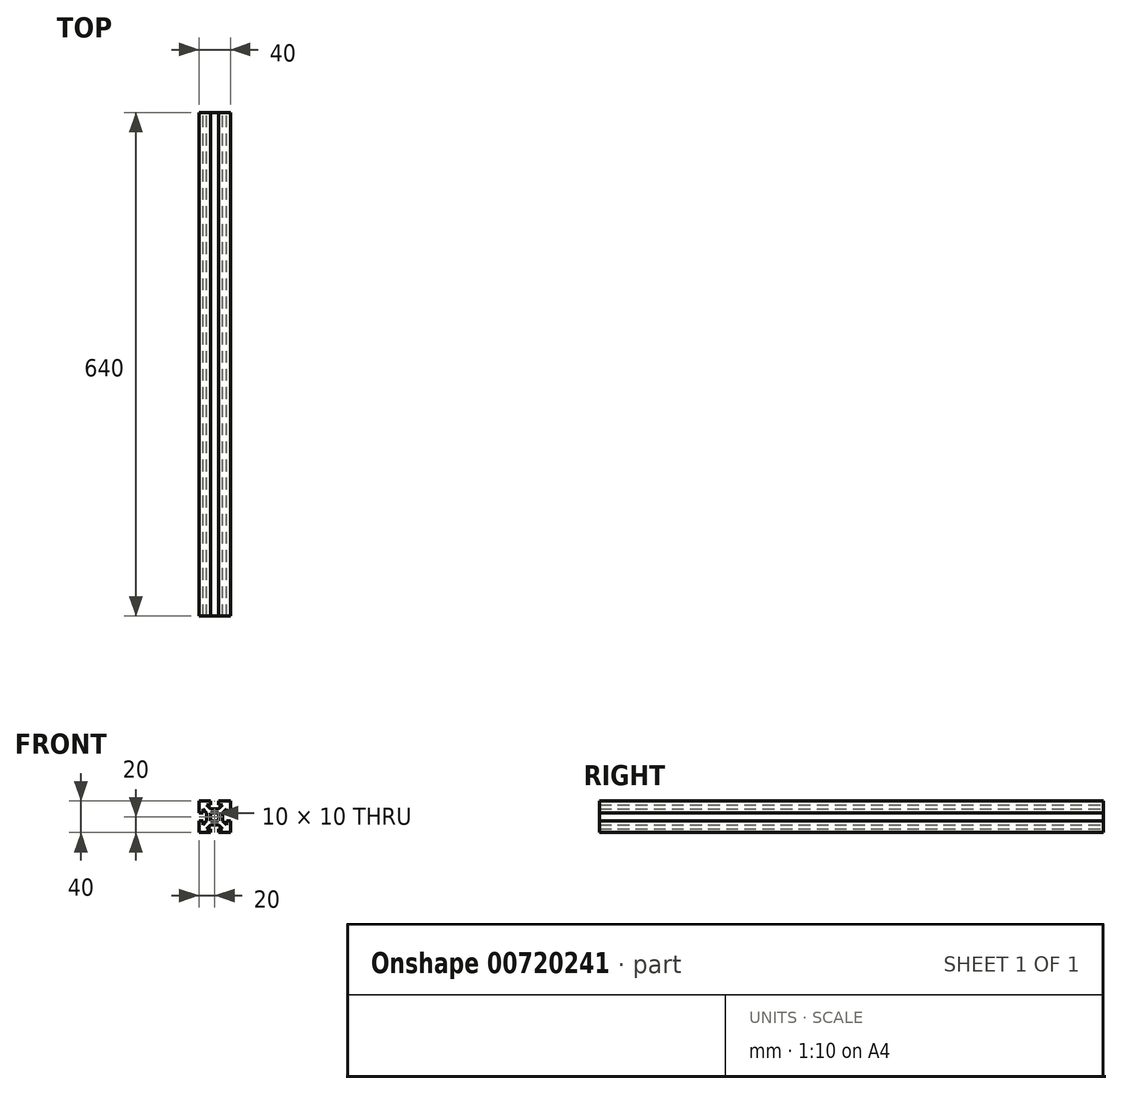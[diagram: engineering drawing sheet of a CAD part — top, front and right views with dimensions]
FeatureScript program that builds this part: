
annotation { "Feature Type Name" : "Feature", "Feature Type Description" : "" }
export const myFeature = defineFeature(function(context is Context, id is Id, definition is map)
    precondition{}
    {
        {
            var Q0;
            Q0=qCreatedBy(makeId("Front.planeOp"),FACE);
            var sketch = newSketch(context, id + "F0", { "sketchPlane" : qUnion([Q0])});
            skLineSegment(sketch, "E0.bottom", {"start": v(20, 20) * mm, "end": v(5, 20) * mm});
            skLineSegment(sketch, "E0.top", {"start": v(20, -20) * mm, "end": v(5, -20) * mm});
            skLineSegment(sketch, "E0.left", {"start": v(20, 20) * mm, "end": v(20, 5) * mm});
            skLineSegment(sketch, "E0.right", {"start": v(-20, 20) * mm, "end": v(-20, 5) * mm});
            skPoint(sketch, "E0.middle", {"position": v(0, 0) * mm});
            skLineSegment(sketch, "E1", {"start": v(0, 20) * mm, "end": v(0, -20) * mm, "construction": true});
            skLineSegment(sketch, "E2", {"start": v(-20, 0) * mm, "end": v(20, 0) * mm, "construction": true});
            skLineSegment(sketch, "E3", {"start": v(-20, 5) * mm, "end": v(-15, 5) * mm});
            skLineSegment(sketch, "E4", {"start": v(-20, -5) * mm, "end": v(-15, -5) * mm});
            skLineSegment(sketch, "E5", {"start": v(-5, 20) * mm, "end": v(-5, 15) * mm});
            skLineSegment(sketch, "E6", {"start": v(5, 20) * mm, "end": v(5, 15) * mm});
            skLineSegment(sketch, "E7", {"start": v(-10, 15) * mm, "end": v(-5, 15) * mm});
            skLineSegment(sketch, "E8", {"start": v(-10, -15) * mm, "end": v(-5, -15) * mm});
            skLineSegment(sketch, "E9", {"start": v(15, 10) * mm, "end": v(15, 5) * mm});
            skLineSegment(sketch, "E10", {"start": v(-15, 10) * mm, "end": v(-10, 5) * mm});
            skLineSegment(sketch, "E11", {"start": v(-10, 15) * mm, "end": v(-5, 10) * mm});
            skLineSegment(sketch, "E12", {"start": v(-15, -10) * mm, "end": v(-10, -5) * mm});
            skLineSegment(sketch, "E13", {"start": v(-10, -15) * mm, "end": v(-5, -10) * mm});
            skLineSegment(sketch, "E14.trimOffspring", {"start": v(20, -5) * mm, "end": v(20, -20) * mm});
            skLineSegment(sketch, "E15.trimOffspring", {"start": v(-20, -5) * mm, "end": v(-20, -20) * mm});
            skLineSegment(sketch, "E16.trimOffspring", {"start": v(-5, -20) * mm, "end": v(-20, -20) * mm});
            skLineSegment(sketch, "E17.trimOffspring", {"start": v(-5, 20) * mm, "end": v(-20, 20) * mm});
            skLineSegment(sketch, "E18.trimOffspring", {"start": v(5, 15) * mm, "end": v(10, 15) * mm});
            skLineSegment(sketch, "E19.trimOffspring", {"start": v(-15, -5) * mm, "end": v(-15, -10) * mm});
            skLineSegment(sketch, "E20.trimOffspring", {"start": v(15, -5) * mm, "end": v(15, -10) * mm});
            skLineSegment(sketch, "E21.trimOffspring", {"start": v(5, -15) * mm, "end": v(10, -15) * mm});
            skLineSegment(sketch, "E22.trimOffspring", {"start": v(-5, 5) * mm, "end": v(-5, -5) * mm});
            skLineSegment(sketch, "E23.trimOffspring", {"start": v(5, 5) * mm, "end": v(5, -5) * mm});
            skLineSegment(sketch, "E24.trimOffspring", {"start": v(15, 5) * mm, "end": v(20, 5) * mm});
            skLineSegment(sketch, "E25.trimOffspring", {"start": v(15, -5) * mm, "end": v(20, -5) * mm});
            skLineSegment(sketch, "E26.trimOffspring", {"start": v(5, -15) * mm, "end": v(5, -20) * mm});
            skLineSegment(sketch, "E27.trimOffspring", {"start": v(-5, -15) * mm, "end": v(-5, -20) * mm});
            skLineSegment(sketch, "E28.trimOffspring", {"start": v(-5, -5) * mm, "end": v(5, -5) * mm});
            skLineSegment(sketch, "E29.trimOffspring", {"start": v(-5, 5) * mm, "end": v(5, 5) * mm});
            skLineSegment(sketch, "E30", {"start": v(10, 5) * mm, "end": v(10, -5) * mm});
            skLineSegment(sketch, "E31", {"start": v(-5, 10) * mm, "end": v(5, 10) * mm});
            skLineSegment(sketch, "E32", {"start": v(-10, 5) * mm, "end": v(-10, -5) * mm});
            skLineSegment(sketch, "E33", {"start": v(-5, -10) * mm, "end": v(5, -10) * mm});
            skLineSegment(sketch, "E34.trimOffspring", {"start": v(-15, 10) * mm, "end": v(-15, 5) * mm});
            skPoint(sketch, "E35.orphan", {"position": v(20, 15) * mm});
            skPoint(sketch, "E36.orphan", {"position": v(20, -15) * mm});
            skPoint(sketch, "E37.orphan", {"position": v(15, -20) * mm});
            skPoint(sketch, "E38.orphan", {"position": v(-15, -20) * mm});
            skLineSegment(sketch, "E39.trimOffspring", {"start": v(-5, 0) * mm, "end": v(0, -5) * mm});
            skLineSegment(sketch, "E40.trimOffspring", {"start": v(-5, 0) * mm, "end": v(0, 5) * mm});
            skLineSegment(sketch, "E41.trimOffspring", {"start": v(0, 5) * mm, "end": v(5, 0) * mm});
            skLineSegment(sketch, "E42.trimOffspring", {"start": v(5, 10) * mm, "end": v(10, 15) * mm});
            skLineSegment(sketch, "E43.trimOffspring", {"start": v(10, 5) * mm, "end": v(15, 10) * mm});
            skLineSegment(sketch, "E44.trimOffspring", {"start": v(10, -5) * mm, "end": v(15, -10) * mm});
            skLineSegment(sketch, "E45.trimOffspring", {"start": v(5, -10) * mm, "end": v(10, -15) * mm});
            skLineSegment(sketch, "E46.trimOffspring", {"start": v(0, -5) * mm, "end": v(5, 0) * mm});
            skSolve(sketch);
        }
        {
            var Q0;
            Q0=makeQuery(id+"F0.imprint","IMPRINT",FACE,{"disambiguationData":[TD([[makeQuery(id+"F0.imprint","IMPRINT",EDGE,{"derivedFrom":sQuery(id+"F0.wireOp",EDGE,"E0.bottom")}),1.0]])]});
            extrude(context, id + "F1", {"entities" : qUnion([Q0]), "depth" : 640 * mm, "offsetDistance" : 25 * mm});
        }
    });
